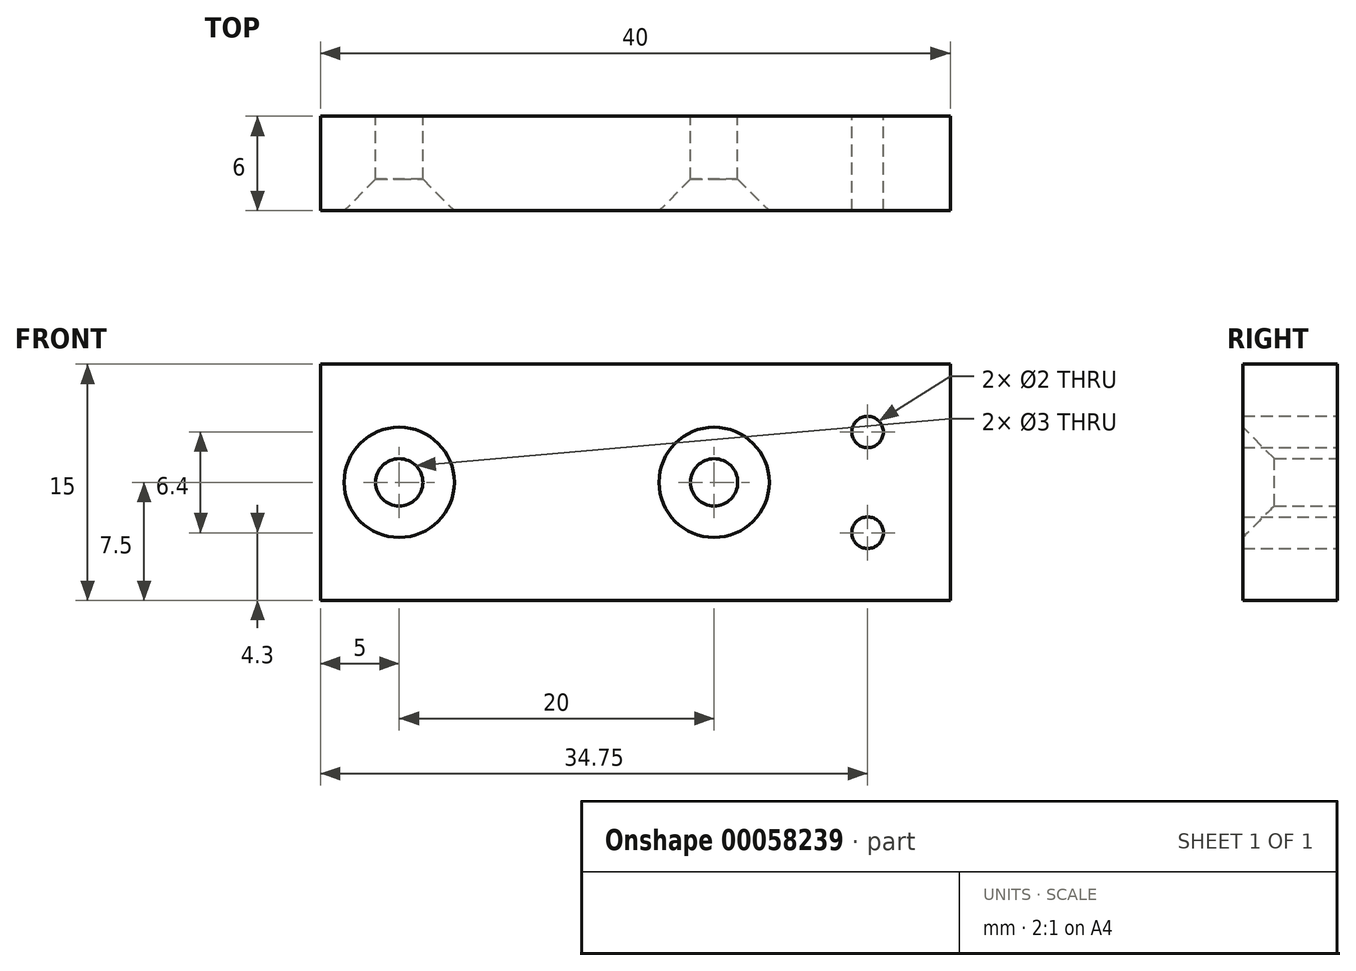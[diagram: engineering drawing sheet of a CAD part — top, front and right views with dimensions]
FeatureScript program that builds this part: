
annotation { "Feature Type Name" : "Feature", "Feature Type Description" : "" }
export const myFeature = defineFeature(function(context is Context, id is Id, definition is map)
    precondition{}
    {
        {
            var Q0;
            Q0=qCreatedBy(makeId("Front.planeOp"),FACE);
            var sketch = newSketch(context, id + "F0", { "sketchPlane" : qUnion([Q0])});
            skLineSegment(sketch, "E0.bottom", {"start": v(20, 7.5) * mm, "end": v(-20, 7.5) * mm});
            skLineSegment(sketch, "E0.top", {"start": v(20, -7.5) * mm, "end": v(-20, -7.5) * mm});
            skLineSegment(sketch, "E0.left", {"start": v(20, 7.5) * mm, "end": v(20, -7.5) * mm});
            skLineSegment(sketch, "E0.right", {"start": v(-20, 7.5) * mm, "end": v(-20, -7.5) * mm});
            skPoint(sketch, "E0.middle", {"position": v(0, 0) * mm});
            skLineSegment(sketch, "E1", {"start": v(-20, 0) * mm, "end": v(0, 0) * mm, "construction": true});
            skLineSegment(sketch, "E2", {"start": v(0, 7.5) * mm, "end": v(0, 0) * mm, "construction": true});
            skCircle(sketch, "E3", {"center": v(-15, 0) * mm, "radius": 1.5 * mm});
            skCircle(sketch, "E4", {"center": v(14.75, 3.2) * mm, "radius": 1 * mm});
            skCircle(sketch, "E5", {"center": v(14.75, -3.2) * mm, "radius": 1 * mm});
            skCircle(sketch, "E6", {"center": v(5, 0) * mm, "radius": 1.5 * mm});
            skSolve(sketch);
        }
        {
            var Q0;
            Q0 = qSketchRegion(id + "F0", true);
            extrude(context, id + "F1", {"entities" : qUnion([Q0]), "depth" : 6 * mm});
        }
        {
            var Q0;
            Q0=makeQuery(id+"F1.opExtrude","CAP_EDGE",EDGE,{"disambiguationData":[OSD([sQuery(id+"F0.wireOp",EDGE,"E3")])],"isStart":false});
            var Q1;
            Q1=makeQuery(id+"F1.opExtrude","CAP_EDGE",EDGE,{"disambiguationData":[OSD([sQuery(id+"F0.wireOp",EDGE,"E6")])],"isStart":false});
            chamfer(context, id + "F2", {"entities" : qUnion([Q0, Q1]), "width" : 2 * mm, "tangentPropagation" : true});
        }
    });
